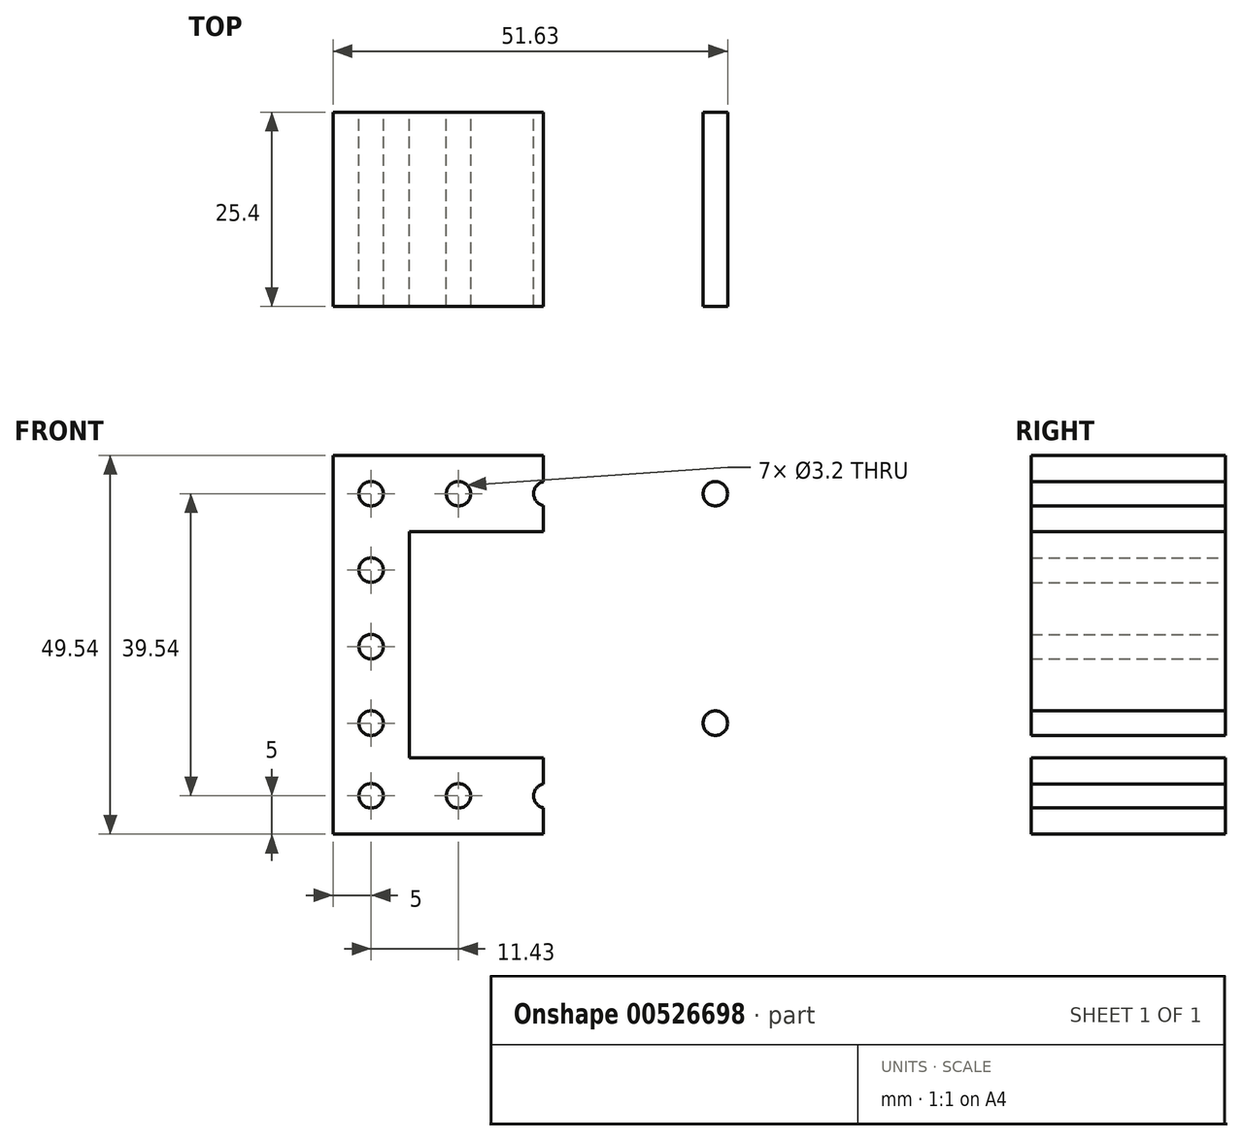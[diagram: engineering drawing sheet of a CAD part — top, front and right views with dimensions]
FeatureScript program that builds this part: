
annotation { "Feature Type Name" : "Feature", "Feature Type Description" : "" }
export const myFeature = defineFeature(function(context is Context, id is Id, definition is map)
    precondition{}
    {
        {
            var Q0;
            Q0=qCreatedBy(makeId("Front.planeOp"),FACE);
            var sketch = newSketch(context, id + "F0", { "sketchPlane" : qUnion([Q0])});
            skLineSegment(sketch, "E0.bottom", {"start": v(0, 0) * mm, "end": v(35.03, 0) * mm});
            skLineSegment(sketch, "E0.top", {"start": v(0, -29.54) * mm, "end": v(35.03, -29.54) * mm});
            skLineSegment(sketch, "E0.left", {"start": v(0, 0) * mm, "end": v(0, -29.54) * mm});
            skLineSegment(sketch, "E0.right", {"start": v(35.03, 0) * mm, "end": v(35.03, -29.54) * mm});
            skLineSegment(sketch, "E1.bottom", {"start": v(-10, 10) * mm, "end": v(45.03, 10) * mm});
            skLineSegment(sketch, "E1.top", {"start": v(-10, -39.54) * mm, "end": v(45.03, -39.54) * mm});
            skLineSegment(sketch, "E1.left", {"start": v(-10, 10) * mm, "end": v(-10, -39.54) * mm});
            skLineSegment(sketch, "E1.right", {"start": v(45.03, 10) * mm, "end": v(45.03, -39.54) * mm});
            skCircle(sketch, "E2", {"center": v(-5, 5) * mm, "radius": 1.6 * mm});
            skCircle(sketch, "E3", {"center": v(-5, -5) * mm, "radius": 1.6 * mm});
            skCircle(sketch, "E4.0.1.0", {"center": v(-5, -15.02) * mm, "radius": 1.6 * mm});
            skCircle(sketch, "E4.0.2.0", {"center": v(-5, -25.02) * mm, "radius": 1.6 * mm});
            skLineSegment(sketch, "E4.direction1", {"start": v(-5, -5) * mm, "end": v(20.4, -5) * mm, "construction": true});
            skLineSegment(sketch, "E4.direction2", {"start": v(-5, -5) * mm, "end": v(-5, -15.02) * mm, "construction": true});
            skLineSegment(sketch, "E5", {"start": v(17.51, 10) * mm, "end": v(17.51, -39.54) * mm});
            skCircle(sketch, "E6.MirrorC", {"center": v(40.03, 5) * mm, "radius": 1.6 * mm});
            skCircle(sketch, "E7.MirrorC", {"center": v(40.03, -5) * mm, "radius": 1.6 * mm});
            skCircle(sketch, "E8.MirrorC", {"center": v(40.03, -15.02) * mm, "radius": 1.6 * mm});
            skCircle(sketch, "E9.MirrorC", {"center": v(40.03, -25.02) * mm, "radius": 1.6 * mm});
            skCircle(sketch, "E10.1.0.0", {"center": v(6.43, 5) * mm, "radius": 1.6 * mm});
            skCircle(sketch, "E10.2.0.0", {"center": v(17.86, 5) * mm, "radius": 1.6 * mm});
            skCircle(sketch, "E10.3.0.0", {"center": v(29.29, 5) * mm, "radius": 1.6 * mm});
            skLineSegment(sketch, "E10.direction1", {"start": v(-5, 5) * mm, "end": v(6.43, 5) * mm, "construction": true});
            skLineSegment(sketch, "E11", {"start": v(-10, -14.77) * mm, "end": v(45.03, -14.77) * mm});
            skCircle(sketch, "E12.MirrorC", {"center": v(6.43, -34.54) * mm, "radius": 1.6 * mm});
            skCircle(sketch, "E13.MirrorC", {"center": v(17.86, -34.54) * mm, "radius": 1.6 * mm});
            skCircle(sketch, "E14.MirrorC", {"center": v(29.29, -34.54) * mm, "radius": 1.6 * mm});
            skCircle(sketch, "E15.MirrorC", {"center": v(40.03, -34.54) * mm, "radius": 1.6 * mm});
            skCircle(sketch, "E16.MirrorC", {"center": v(-5, -34.54) * mm, "radius": 1.6 * mm});
            skSolve(sketch);
        }
        {
            var Q0;
            Q0=makeQuery(id+"F0.imprint","IMPRINT",FACE,{"disambiguationData":[TD([[makeQuery(id+"F0.imprint","IMPRINT",EDGE,{"derivedFrom":sQuery(id+"F0.wireOp",EDGE,"E2")}),-1.0]])]});
            var Q1;
            Q1=makeQuery(id+"F0.imprint","IMPRINT",FACE,{"disambiguationData":[TD([[makeQuery(id+"F0.imprint","IMPRINT",EDGE,{"derivedFrom":sQuery(id+"F0.wireOp",EDGE,"E6.MirrorC")}),1.0]])]});
            var Q2;
            Q2=makeQuery(id+"F0.imprint","IMPRINT",FACE,{"disambiguationData":[TD([[makeQuery(id+"F0.imprint","IMPRINT",EDGE,{"derivedFrom":sQuery(id+"F0.wireOp",EDGE,"E9.MirrorC")}),1.0]])]});
            var Q3;
            Q3=makeQuery(id+"F0.imprint","IMPRINT",FACE,{"disambiguationData":[TD([[makeQuery(id+"F0.imprint","IMPRINT",EDGE,{"derivedFrom":sQuery(id+"F0.wireOp",EDGE,"E4.0.2.0")}),-1.0]])]});
            extrude(context, id + "F1", {"entities" : qUnion([Q0, Q1, Q2, Q3]), "depth" : 25.4 * mm, "offsetDistance" : 25.4 * mm});
        }
    });
